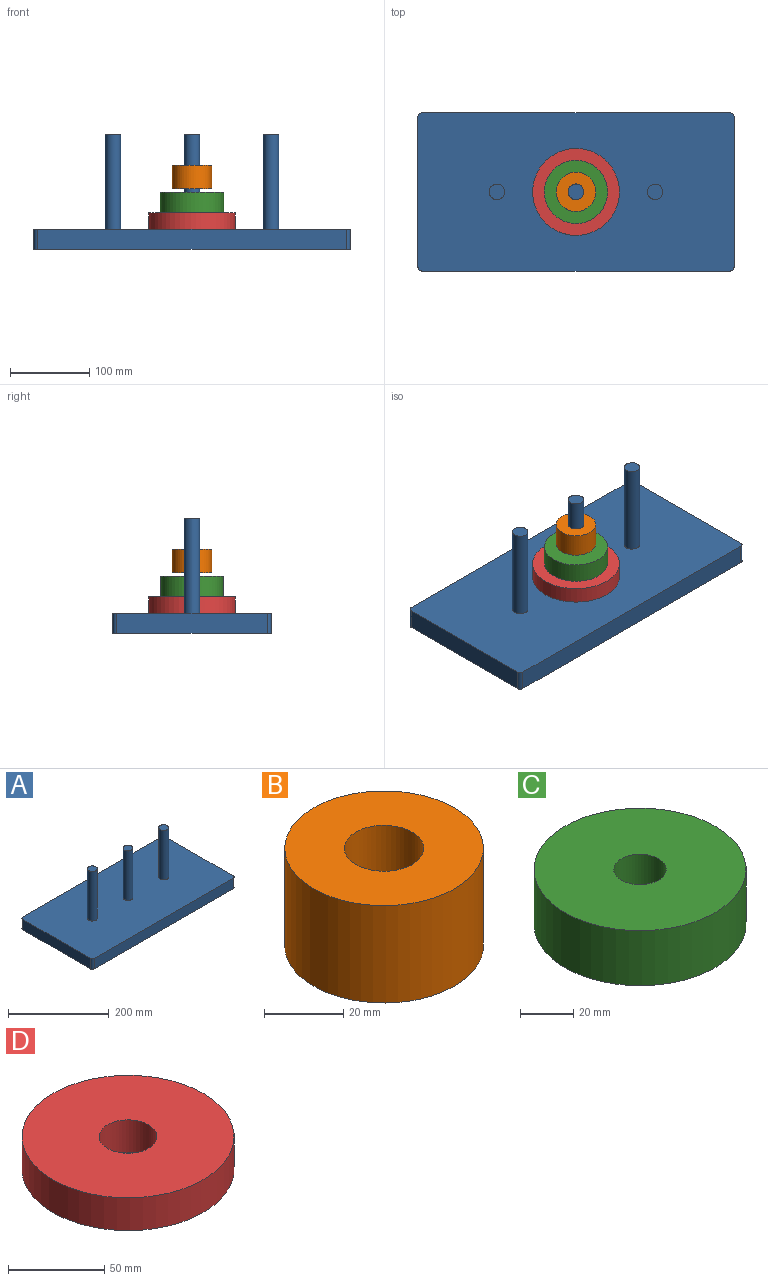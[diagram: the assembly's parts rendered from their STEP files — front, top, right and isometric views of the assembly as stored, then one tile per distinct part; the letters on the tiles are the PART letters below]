
ASSEMBLY  parts=4 mates=3
PART A: 16 faces, bbox 400x200x145.4 mm
  f0: plane 189.84x25.4mm, normal (-1,0,0), area 4821.9mm2, adj f4,f5,f6,f9
  f1: plane 389.84x25.4mm, normal (0,-1,0), area 9901.9mm2, adj f4,f5,f6,f7
  f2: plane 189.84x25.4mm, normal (1,0,0), area 4821.9mm2, adj f4,f5,f7,f8
  f3: plane 389.84x25.4mm, normal (0,1,0), area 9901.9mm2, adj f4,f5,f8,f9
  f4: plane 400x200mm, normal (0,0,1), area 79081.9mm2, adj f0,f1,f2,f3,f6,f7,f8,f9
  f5: plane 400x200mm, normal (0,0,-1), area 79977.8mm2, adj f0,f1,f2,f3,f6,f7,f8,f9
  f6: cylinder r=5.08mm len=25.4mm, axis (0,0,-1), area 202.7mm2, adj f0,f1,f4,f5
  f7: cylinder r=5.08mm len=25.4mm, axis (0,0,1), area 202.7mm2, adj f1,f2,f4,f5
  f8: cylinder r=5.08mm len=25.4mm, axis (0,0,-1), area 202.7mm2, adj f2,f3,f4,f5
  f9: cylinder r=5.08mm len=25.4mm, axis (0,0,1), area 202.7mm2, adj f0,f3,f4,f5
  f10: cylinder r=9.75mm len=120mm, axis (0,0,-1), area 7351.3mm2, adj f4,f11
  f11: plane 19.5x19.5mm, normal (0,0,1), area 298.6mm2, adj f10
  f12: cylinder r=9.75mm len=120mm, axis (0,0,-1), area 7351.3mm2, adj f4,f13
  f13: plane 19.5x19.5mm, normal (0,0,1), area 298.6mm2, adj f12
  f14: cylinder r=9.75mm len=120mm, axis (0,0,-1), area 7351.3mm2, adj f4,f15
  f15: plane 19.5x19.5mm, normal (0,0,1), area 298.6mm2, adj f14
PART B: 4 faces, bbox 50x50x30 mm
  f0: cylinder r=10mm len=30mm, axis (0,0,-1), area 1885mm2, adj f2,f3
  f1: cylinder r=25mm len=50mm, axis (0,0,-1), area 4712.4mm2, adj f2,f3
  f2: plane 50x50mm, normal (0,0,1), area 1649.3mm2, adj f0,f1
  f3: plane 50x50mm, normal (0,0,-1), area 1649.3mm2, adj f0,f1
PART C: 4 faces, bbox 80x80x25.4 mm
  f0: cylinder r=9.92mm len=25.4mm, axis (0,0,-1), area 1582.8mm2, adj f2,f3
  f1: cylinder r=40mm len=80mm, axis (0,0,-1), area 6383.7mm2, adj f2,f3
  f2: plane 80x80mm, normal (0,0,1), area 4717.5mm2, adj f0,f1
  f3: plane 80x80mm, normal (0,0,-1), area 4717.5mm2, adj f0,f1
PART D: 4 faces, bbox 110x110x20.8 mm
  f0: cylinder r=15mm len=30mm, axis (0,0,-1), area 1963mm2, adj f2,f3
  f1: cylinder r=55mm len=110mm, axis (0,0,-1), area 7197.6mm2, adj f2,f3
  f2: plane 110x110mm, normal (0,0,1), area 8796.5mm2, adj f0,f1
  f3: plane 110x110mm, normal (0,0,-1), area 8796.5mm2, adj f0,f1
PLACE A t=(-71.52,16.01,-17.9)mm
PLACE B t=(-71.52,16.01,58.92)mm
PLACE C t=(-71.52,16.01,29.04)mm
PLACE D t=(-71.52,16.01,7.5)mm
MATE slider C.f0 <-> A.f12  axis (0,0,-1) through (-71.52,16.01,29.04)mm
MATE slider B.f0 <-> A.f12  axis (0,0,1) through (-71.52,16.01,88.92)mm
MATE slider D.f0 <-> A.f12  axis (0,0,-1) through (-71.52,16.01,7.5)mm
